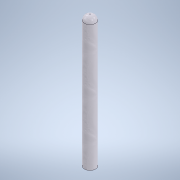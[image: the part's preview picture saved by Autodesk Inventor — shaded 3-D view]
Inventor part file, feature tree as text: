
AUTODESK INVENTOR PART (.ipt)
format: ipt  version: 2020 (Build 240168000, 168)  size: 103,936 bytes
history: native  units: mm
features: revolve x1, sketch x1
ambient origin geometry x8: Origin, YZ Plane, XZ Plane, XY Plane, X Axis, Y Axis, Z Axis, Center Point
bodies: Solid1 (feature_tree)
feature tree (2):
  revolve  "Revolution1"  [1 undecoded]
  sketch  "Sketch3"  dims[d1=6.35mm d2=150.0mm d3=6.0mm d4=90.0deg]
note: 1 required parameter value undecoded (feature->parameter linkage not recoverable at this tier; creation-order binding heuristic only, values carry confidence <= 0.55)
